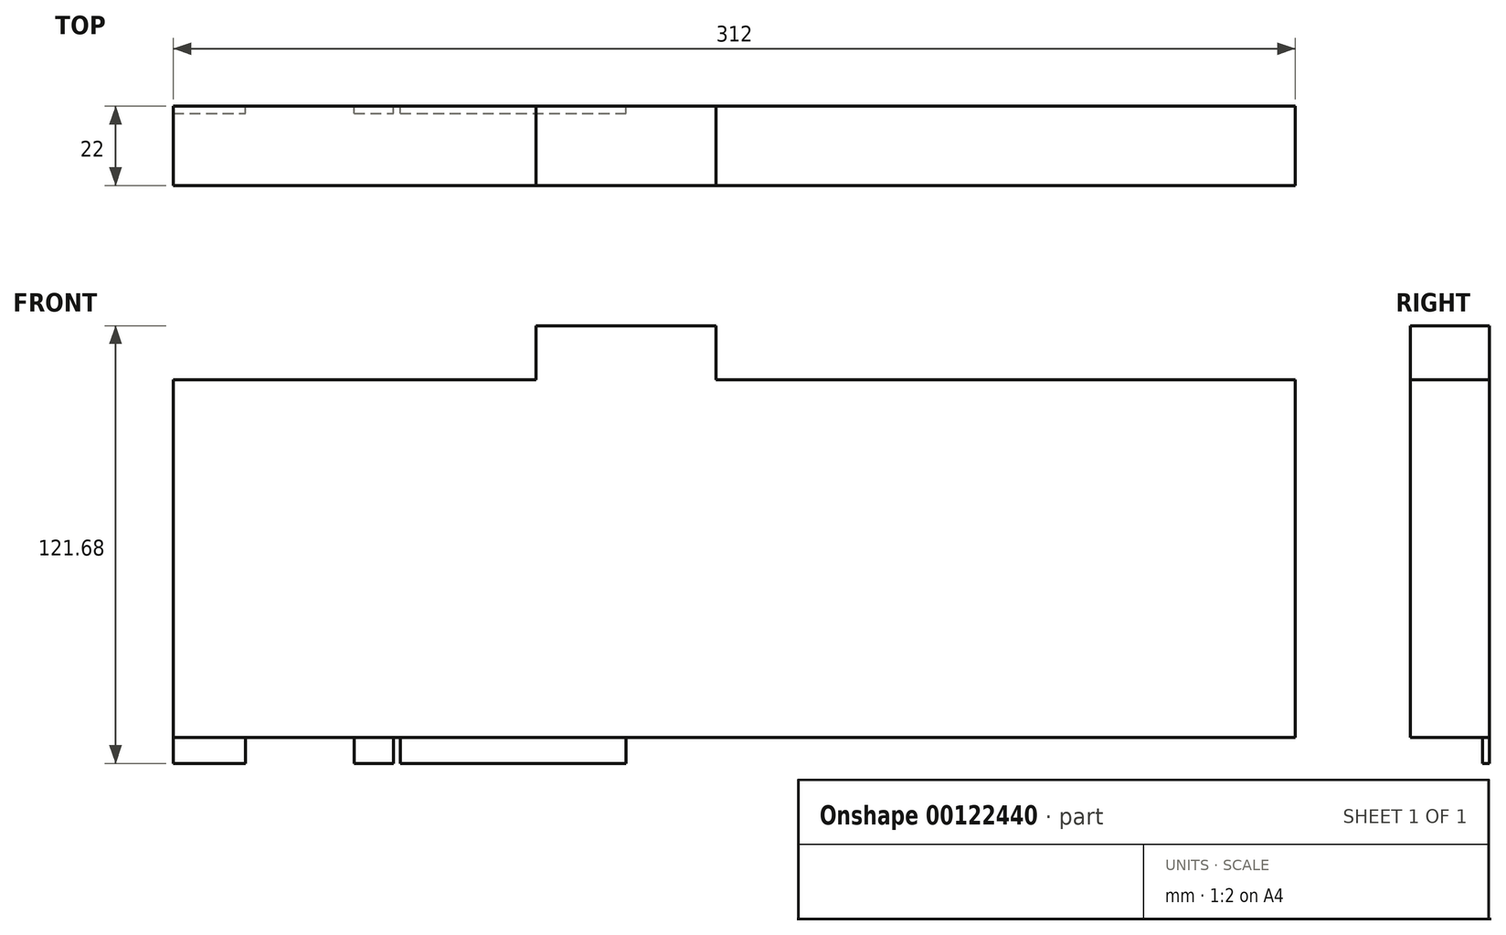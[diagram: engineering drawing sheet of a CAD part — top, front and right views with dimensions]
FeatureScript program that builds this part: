
annotation { "Feature Type Name" : "Feature", "Feature Type Description" : "" }
export const myFeature = defineFeature(function(context is Context, id is Id, definition is map)
    precondition{}
    {
        {
            var Q0;
            Q0=qCreatedBy(makeId("Front.planeOp"),FACE);
            var sketch = newSketch(context, id + "F0", { "sketchPlane" : qUnion([Q0])});
            skLineSegment(sketch, "E0.bottom", {"start": v(0, 0) * mm, "end": v(20.08, 0) * mm});
            skLineSegment(sketch, "E0.top", {"start": v(0, 106.68) * mm, "end": v(312, 106.68) * mm});
            skLineSegment(sketch, "E0.left", {"start": v(0, 0) * mm, "end": v(0, 106.68) * mm});
            skLineSegment(sketch, "E0.right", {"start": v(312, 7.24) * mm, "end": v(312, 106.68) * mm});
            skLineSegment(sketch, "E1", {"start": v(20.08, 0) * mm, "end": v(20.08, 7.24) * mm});
            skLineSegment(sketch, "E2", {"start": v(20.08, 7.24) * mm, "end": v(50.3, 7.24) * mm});
            skLineSegment(sketch, "E3", {"start": v(63.14, 7.24) * mm, "end": v(63.14, 0) * mm});
            skLineSegment(sketch, "E4", {"start": v(125.91, 0) * mm, "end": v(125.91, 7.24) * mm});
            skLineSegment(sketch, "E5", {"start": v(125.91, 7.24) * mm, "end": v(312, 7.24) * mm});
            skLineSegment(sketch, "E6.trimOffspring", {"start": v(63.14, 0) * mm, "end": v(125.91, 0) * mm});
            skLineSegment(sketch, "E7", {"start": v(61.3, 7.24) * mm, "end": v(61.3, 0) * mm});
            skLineSegment(sketch, "E8", {"start": v(61.3, 0) * mm, "end": v(50.3, 0) * mm});
            skLineSegment(sketch, "E9", {"start": v(50.3, 0) * mm, "end": v(50.3, 7.24) * mm});
            skLineSegment(sketch, "E10.trimOffspring", {"start": v(61.3, 7.24) * mm, "end": v(63.14, 7.24) * mm});
            skSolve(sketch);
        }
        {
            var Q0;
            Q0 = qSketchRegion(id + "F0", true);
            extrude(context, id + "F1", {"entities" : qUnion([Q0]), "depth" : 2 * mm});
        }
        {
            var Q0;
            Q0=makeQuery(id+"F1.opExtrude","CAP_FACE",FACE,{"disambiguationData":[OSD([sQuery(id+"F0.wireOp",EDGE,"E0.bottom"),sQuery(id+"F0.wireOp",EDGE,"E0.top"),sQuery(id+"F0.wireOp",EDGE,"E0.left"),sQuery(id+"F0.wireOp",EDGE,"E0.right"),sQuery(id+"F0.wireOp",EDGE,"E1"),sQuery(id+"F0.wireOp",EDGE,"E2"),sQuery(id+"F0.wireOp",EDGE,"E3"),sQuery(id+"F0.wireOp",EDGE,"E4"),sQuery(id+"F0.wireOp",EDGE,"E5"),sQuery(id+"F0.wireOp",EDGE,"E6.trimOffspring"),sQuery(id+"F0.wireOp",EDGE,"E7"),sQuery(id+"F0.wireOp",EDGE,"E8"),sQuery(id+"F0.wireOp",EDGE,"E9"),sQuery(id+"F0.wireOp",EDGE,"E10.trimOffspring")])],"isStart":false});
            var sketch = newSketch(context, id + "F2", { "sketchPlane" : qUnion([Q0])});
            skLineSegment(sketch, "E11.bottom", {"start": v(0, 106.68) * mm, "end": v(312, 106.68) * mm});
            skLineSegment(sketch, "E11.top", {"start": v(0, 7.24) * mm, "end": v(312, 7.24) * mm});
            skLineSegment(sketch, "E11.left", {"start": v(0, 106.68) * mm, "end": v(0, 7.24) * mm});
            skLineSegment(sketch, "E11.right", {"start": v(312, 106.68) * mm, "end": v(312, 7.24) * mm});
            skSolve(sketch);
        }
        {
            var Q0;
            Q0 = qSketchRegion(id + "F2", true);
            extrude(context, id + "F3", {"entities" : qUnion([Q0]), "operationType" : NewBodyOperationType.ADD, "depth" : 20 * mm});
        }
        {
            var Q0;
            Q0=makeQuery(id+"F1.opExtrude","CAP_FACE",FACE,{"disambiguationData":[OSD([sQuery(id+"F0.wireOp",EDGE,"E0.bottom"),sQuery(id+"F0.wireOp",EDGE,"E0.top"),sQuery(id+"F0.wireOp",EDGE,"E0.left"),sQuery(id+"F0.wireOp",EDGE,"E0.right"),sQuery(id+"F0.wireOp",EDGE,"E1"),sQuery(id+"F0.wireOp",EDGE,"E2"),sQuery(id+"F0.wireOp",EDGE,"E3"),sQuery(id+"F0.wireOp",EDGE,"E4"),sQuery(id+"F0.wireOp",EDGE,"E5"),sQuery(id+"F0.wireOp",EDGE,"E6.trimOffspring"),sQuery(id+"F0.wireOp",EDGE,"E7"),sQuery(id+"F0.wireOp",EDGE,"E8"),sQuery(id+"F0.wireOp",EDGE,"E9"),sQuery(id+"F0.wireOp",EDGE,"E10.trimOffspring")])],"isStart":true});
            var sketch = newSketch(context, id + "F4", { "sketchPlane" : qUnion([Q0])});
            skLineSegment(sketch, "E12.bottom", {"start": v(-100.91, 106.68) * mm, "end": v(-150.91, 106.68) * mm});
            skLineSegment(sketch, "E12.top", {"start": v(-100.91, 121.68) * mm, "end": v(-150.91, 121.68) * mm});
            skLineSegment(sketch, "E12.left", {"start": v(-100.91, 106.68) * mm, "end": v(-100.91, 121.68) * mm});
            skLineSegment(sketch, "E12.right", {"start": v(-150.91, 106.68) * mm, "end": v(-150.91, 121.68) * mm});
            skSolve(sketch);
        }
        {
            var Q0;
            Q0 = qSketchRegion(id + "F4", true);
            extrude(context, id + "F5", {"entities" : qUnion([Q0]), "operationType" : NewBodyOperationType.ADD, "oppositeDirection" : true, "depth" : 22 * mm});
        }
    });
